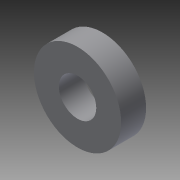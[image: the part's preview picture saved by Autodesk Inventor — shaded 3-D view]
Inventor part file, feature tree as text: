
AUTODESK INVENTOR PART (.ipt)
format: ipt  version: 2013 (Build 170138000, 138)  size: 77,312 bytes
history: native  units: in
note: dims shown in document units (in); Inventor stores cm internally (conversion verified against a paired STEP export)
features: extrude x1, sketch x1
ambient origin geometry x8: Origin, YZ Plane, XZ Plane, XY Plane, X Axis, Y Axis, Z Axis, Center Point
bodies: Solid1 (feature_tree)
feature tree (2):
  extrude  "Extrusion1"  Depth=0.4724in
  sketch  "Sketch1"  dims[d0=1.1024in d2=0.4724in d3=0.315in d4=0.0in]
